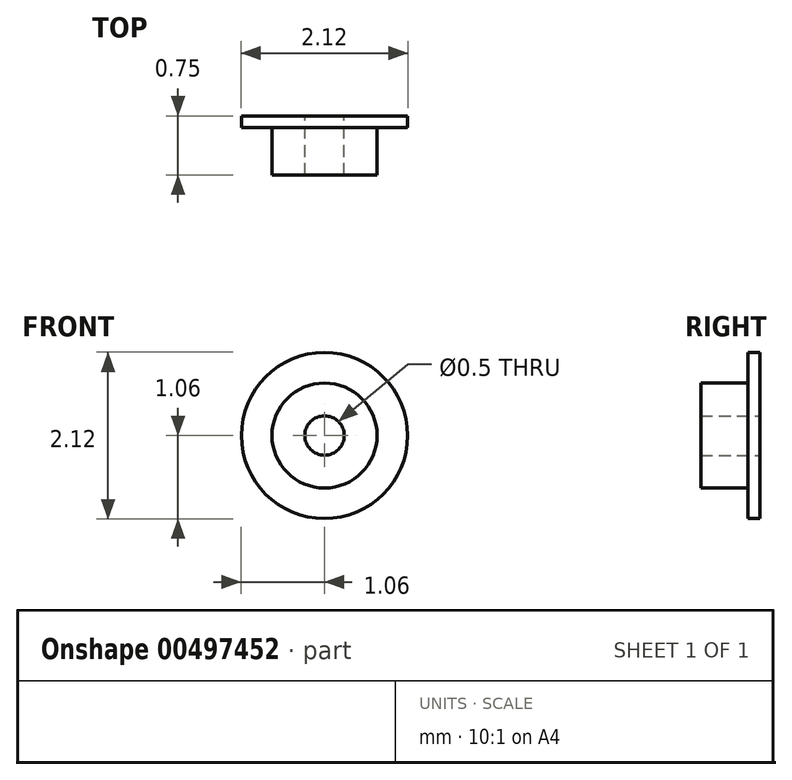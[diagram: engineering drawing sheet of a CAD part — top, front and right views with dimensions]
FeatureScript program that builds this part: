
annotation { "Feature Type Name" : "Feature", "Feature Type Description" : "" }
export const myFeature = defineFeature(function(context is Context, id is Id, definition is map)
    precondition{}
    {
        {
            var Q0;
            Q0=qCreatedBy(makeId("Front.planeOp"),FACE);
            var sketch = newSketch(context, id + "F0", { "sketchPlane" : qUnion([Q0])});
            skCircle(sketch, "E0", {"center": v(0, 0) * mm, "radius": 1.06 * mm});
            skSolve(sketch);
        }
        {
            var Q0;
            Q0 = qSketchRegion(id + "F0", true);
            extrude(context, id + "F1", {"entities" : qUnion([Q0]), "depth" : .15 * mm});
        }
        {
            var Q0;
            Q0=makeQuery(id+"F1.opExtrude","CAP_FACE",FACE,{"disambiguationData":[OSD([sQuery(id+"F0.wireOp",EDGE,"E0")])],"isStart":false});
            var sketch = newSketch(context, id + "F2", { "sketchPlane" : qUnion([Q0])});
            skCircle(sketch, "E1", {"center": v(0, 0) * mm, "radius": 0.67 * mm});
            skSolve(sketch);
        }
        {
            var Q0;
            Q0 = qSketchRegion(id + "F2", true);
            extrude(context, id + "F3", {"entities" : qUnion([Q0]), "operationType" : NewBodyOperationType.ADD, "depth" : .6 * mm});
        }
        {
            var Q0;
            Q0=makeQuery(id+"F1.opExtrude","CAP_FACE",FACE,{"disambiguationData":[OSD([sQuery(id+"F0.wireOp",EDGE,"E0")])],"isStart":true});
            var sketch = newSketch(context, id + "F4", { "sketchPlane" : qUnion([Q0])});
            skCircle(sketch, "E2", {"center": v(0, 0) * mm, "radius": 0.25 * mm});
            skSolve(sketch);
        }
        {
            var Q0;
            Q0 = qSketchRegion(id + "F4", true);
            extrude(context, id + "F5", {"entities" : qUnion([Q0]), "operationType" : NewBodyOperationType.REMOVE, "oppositeDirection" : true, "depth" : 25 * mm});
        }
    });
